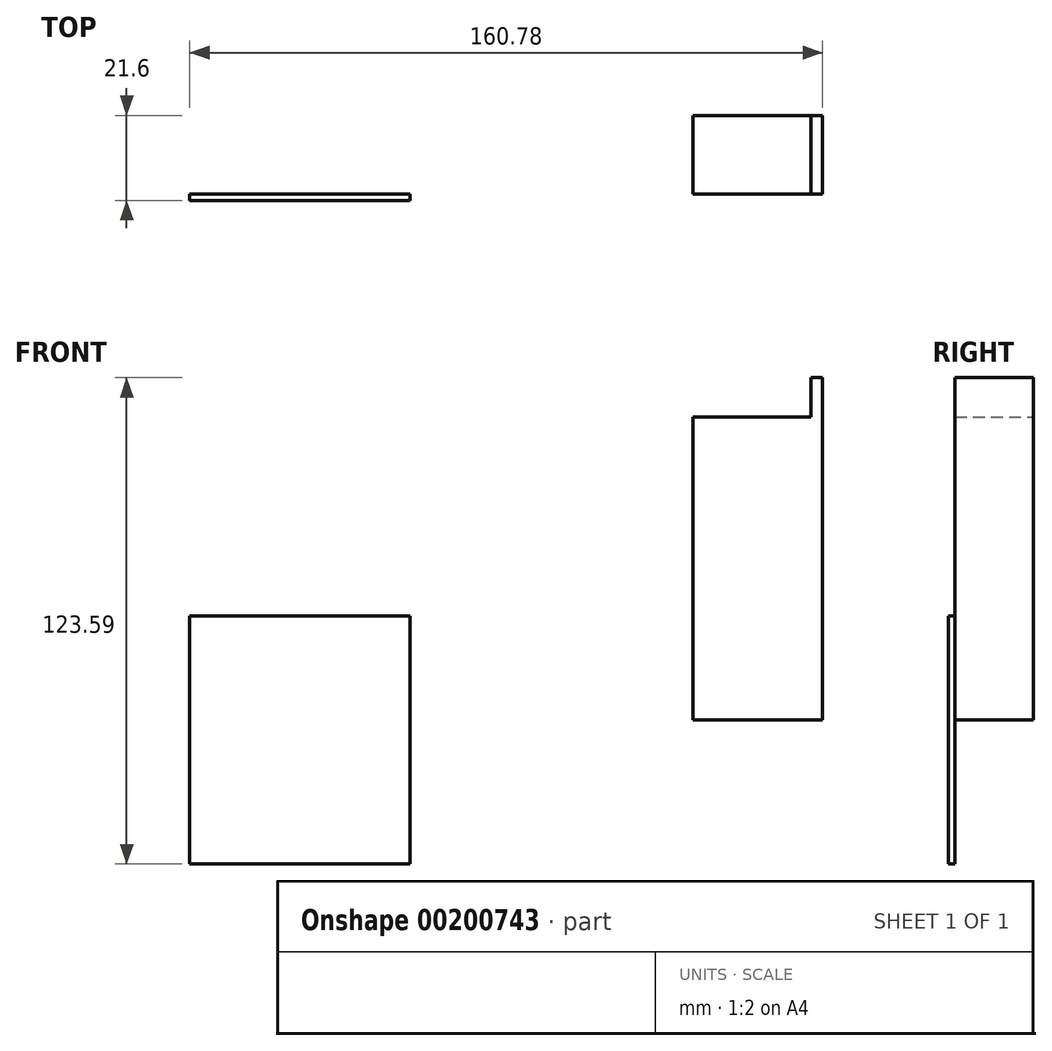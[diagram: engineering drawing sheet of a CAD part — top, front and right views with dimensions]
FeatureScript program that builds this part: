
annotation { "Feature Type Name" : "Feature", "Feature Type Description" : "" }
export const myFeature = defineFeature(function(context is Context, id is Id, definition is map)
    precondition{}
    {
        {
            var Q0;
            Q0=qCreatedBy(makeId("Front.planeOp"),FACE);
            var sketch = newSketch(context, id + "F0", { "sketchPlane" : qUnion([Q0]), "asVersion" : FeatureScriptVersionNumber.V581_REMOVE_HELIX_CONTROL_VISIBILITY});
            skLineSegment(sketch, "E0.bottom", {"start": v(-127.78, 26.4) * mm, "end": v(-71.78, 26.4) * mm});
            skLineSegment(sketch, "E0.top", {"start": v(-127.78, -36.6) * mm, "end": v(-71.78, -36.6) * mm});
            skLineSegment(sketch, "E0.left", {"start": v(-127.78, 26.4) * mm, "end": v(-127.78, -36.6) * mm});
            skLineSegment(sketch, "E0.right", {"start": v(-71.78, 26.4) * mm, "end": v(-71.78, -36.6) * mm});
            skSolve(sketch);
        }
        {
            var Q0;
            Q0 = qSketchRegion(id + "F0", true);
            extrude(context, id + "F1", {"entities" : qUnion([Q0]), "depth" : 1.6 * mm});
        }
        {
            var Q0;
            Q0=qCreatedBy(makeId("Top.planeOp"),FACE);
            var sketch = newSketch(context, id + "F2", { "sketchPlane" : qUnion([Q0]), "asVersion" : FeatureScriptVersionNumber.V581_REMOVE_HELIX_CONTROL_VISIBILITY});
            skLineSegment(sketch, "E1.bottom", {"start": v(0, 0) * mm, "end": v(33, 0) * mm});
            skLineSegment(sketch, "E1.top", {"start": v(0, 20) * mm, "end": v(33, 20) * mm});
            skLineSegment(sketch, "E1.left", {"start": v(0, 0) * mm, "end": v(0, 20) * mm});
            skLineSegment(sketch, "E1.right", {"start": v(33, 0) * mm, "end": v(33, 20) * mm});
            skSolve(sketch);
        }
        {
            var Q0;
            Q0 = qSketchRegion(id + "F2", true);
            extrude(context, id + "F3", {"entities" : qUnion([Q0]), "depth" : 77 * mm});
        }
        {
            var Q0;
            Q0=makeQuery(id+"F3.opExtrude","CAP_FACE",FACE,{"disambiguationData":[OSD([sQuery(id+"F2.wireOp",EDGE,"E1.bottom"),sQuery(id+"F2.wireOp",EDGE,"E1.top"),sQuery(id+"F2.wireOp",EDGE,"E1.left"),sQuery(id+"F2.wireOp",EDGE,"E1.right")])],"isStart":false});
            var sketch = newSketch(context, id + "F4", { "sketchPlane" : qUnion([Q0]), "asVersion" : FeatureScriptVersionNumber.V581_REMOVE_HELIX_CONTROL_VISIBILITY});
            skLineSegment(sketch, "E2.bottom", {"start": v(33, 20) * mm, "end": v(30, 20) * mm});
            skLineSegment(sketch, "E2.top", {"start": v(33, 0) * mm, "end": v(30, 0) * mm});
            skLineSegment(sketch, "E2.left", {"start": v(33, 20) * mm, "end": v(33, 0) * mm});
            skLineSegment(sketch, "E2.right", {"start": v(30, 20) * mm, "end": v(30, 0) * mm});
            skSolve(sketch);
        }
        {
            var Q0;
            Q0 = qSketchRegion(id + "F4", true);
            extrude(context, id + "F5", {"entities" : qUnion([Q0]), "operationType" : NewBodyOperationType.ADD, "depth" : 10 * mm});
        }
    });
